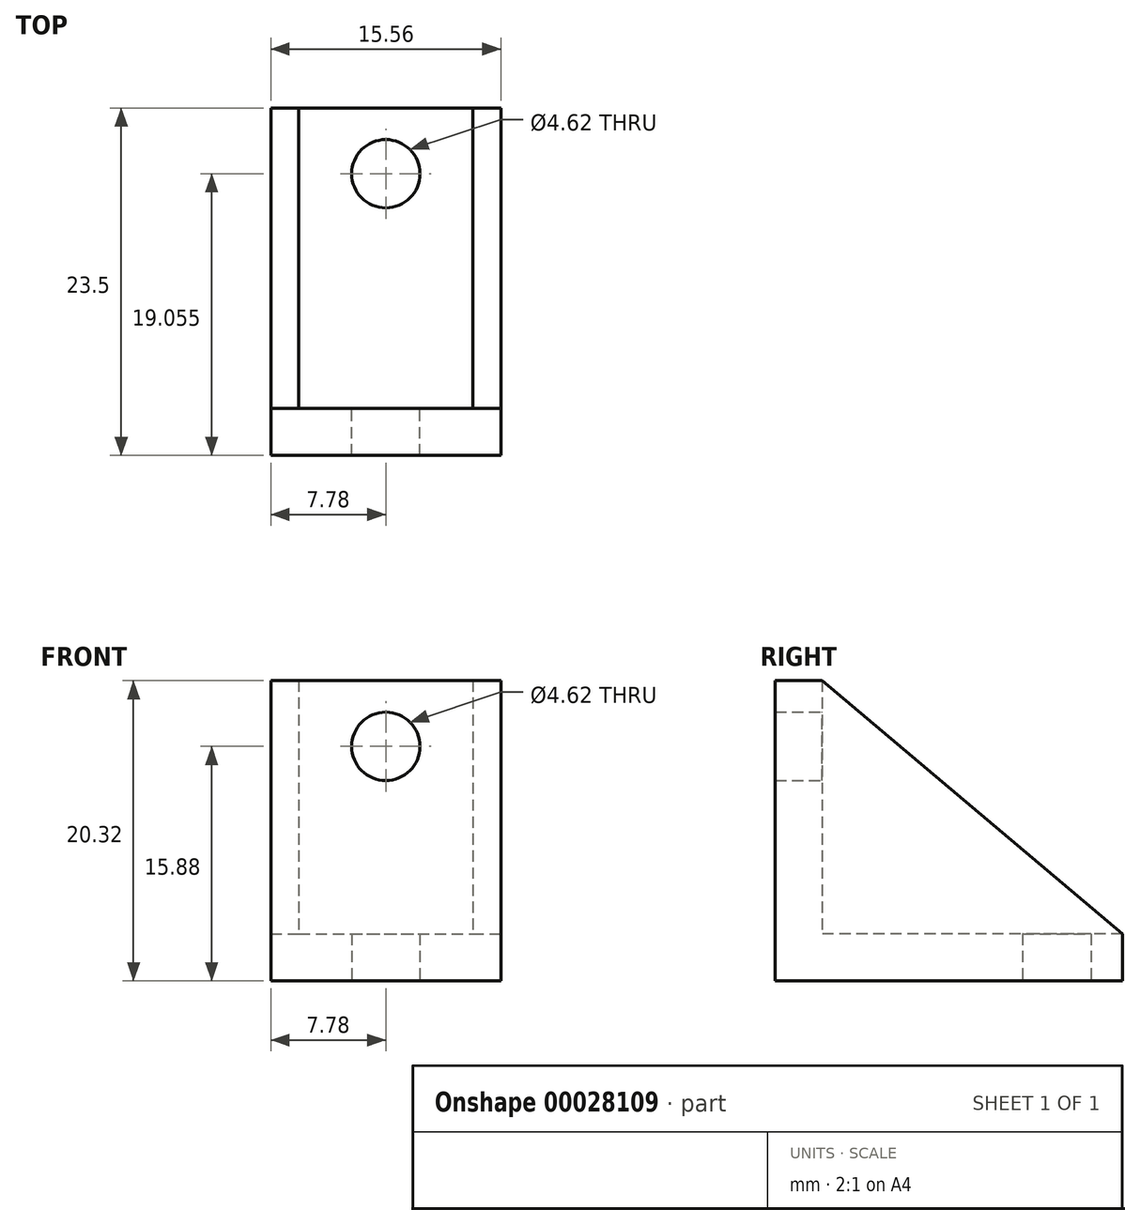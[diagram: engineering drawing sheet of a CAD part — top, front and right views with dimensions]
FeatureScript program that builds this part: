
annotation { "Feature Type Name" : "Feature", "Feature Type Description" : "" }
export const myFeature = defineFeature(function(context is Context, id is Id, definition is map)
    precondition{}
    {
        {
            var Q0;
            Q0=qCreatedBy(makeId("Front.planeOp"),FACE);
            var sketch = newSketch(context, id + "F0", { "sketchPlane" : qUnion([Q0])});
            skLineSegment(sketch, "E0.bottom", {"start": v(-31.66, 5.56) * mm, "end": v(-16.1, 5.56) * mm});
            skLineSegment(sketch, "E0.top", {"start": v(-31.66, -14.76) * mm, "end": v(-16.1, -14.76) * mm});
            skLineSegment(sketch, "E0.left", {"start": v(-31.66, 5.56) * mm, "end": v(-31.66, -14.76) * mm});
            skLineSegment(sketch, "E0.right", {"start": v(-16.1, 5.56) * mm, "end": v(-16.1, -14.76) * mm});
            skLineSegment(sketch, "E1.bottom", {"start": v(-31.66, -14.76) * mm, "end": v(-16.1, -14.76) * mm, "construction": true});
            skLineSegment(sketch, "E1.top", {"start": v(-31.66, -17.93) * mm, "end": v(-16.1, -17.93) * mm, "construction": true});
            skLineSegment(sketch, "E1.left", {"start": v(-31.66, -14.76) * mm, "end": v(-31.66, -17.93) * mm, "construction": true});
            skLineSegment(sketch, "E1.right", {"start": v(-16.1, -14.76) * mm, "end": v(-16.1, -17.93) * mm, "construction": true});
            skLineSegment(sketch, "E2", {"start": v(-23.88, -17.93) * mm, "end": v(-23.88, 1.12) * mm, "construction": true});
            skCircle(sketch, "E3", {"center": v(-23.88, 1.12) * mm, "radius": 2.31 * mm});
            skSolve(sketch);
        }
        {
            var Q0;
            Q0=makeQuery(id+"F0.imprint","IMPRINT",FACE,{"disambiguationData":[TD([[makeQuery(id+"F0.imprint","IMPRINT",EDGE,{"derivedFrom":sQuery(id+"F0.wireOp",EDGE,"E0.bottom")}),-1.0]])]});
            extrude(context, id + "F1", {"entities" : qUnion([Q0]), "depth" : 3.17 * mm});
        }
        {
            var Q0;
            Q0=makeQuery(id+"F1.opExtrude","CAP_FACE",FACE,{"disambiguationData":[OSD([sQuery(id+"F0.wireOp",EDGE,"E0.bottom"),sQuery(id+"F0.wireOp",EDGE,"E0.top"),sQuery(id+"F0.wireOp",EDGE,"E0.left"),sQuery(id+"F0.wireOp",EDGE,"E0.right"),sQuery(id+"F0.wireOp",EDGE,"E3")])],"isStart":true});
            var sketch = newSketch(context, id + "F2", { "sketchPlane" : qUnion([Q0])});
            skLineSegment(sketch, "E4.bottom", {"start": v(31.66, -14.76) * mm, "end": v(16.1, -14.76) * mm});
            skLineSegment(sketch, "E4.top", {"start": v(31.66, -11.58) * mm, "end": v(16.1, -11.58) * mm});
            skLineSegment(sketch, "E4.left", {"start": v(31.66, -14.76) * mm, "end": v(31.66, -11.58) * mm});
            skLineSegment(sketch, "E4.right", {"start": v(16.1, -14.76) * mm, "end": v(16.1, -11.58) * mm});
            skSolve(sketch);
        }
        {
            var Q0;
            Q0=makeQuery(id+"F2.imprint","IMPRINT",FACE,{"disambiguationData":[TD([[makeQuery(id+"F2.imprint","IMPRINT",EDGE,{"derivedFrom":sQuery(id+"F2.wireOp",EDGE,"E4.bottom")}),-1.0]])]});
            extrude(context, id + "F3", {"entities" : qUnion([Q0]), "operationType" : NewBodyOperationType.ADD, "depth" : 20.32 * mm});
        }
        {
            var Q0;
            Q0=makeQuery(id+"F3.boolean.opBoolean","MERGE",FACE,{"derivedFrom":[makeQuery(id+"F1.opExtrude","SWEPT_FACE",FACE,{"disambiguationData":[OSD([sQuery(id+"F0.wireOp",EDGE,"E0.top")])]}),makeQuery(id+"F3.opExtrude","SWEPT_FACE",FACE,{"disambiguationData":[OSD([sQuery(id+"F2.wireOp",EDGE,"E4.bottom")])]})]});
            var sketch = newSketch(context, id + "F4", { "sketchPlane" : qUnion([Q0])});
            skLineSegment(sketch, "E5", {"start": v(-23.88, 3.18) * mm, "end": v(-23.88, -15.88) * mm, "construction": true});
            skPoint(sketch, "E5.endSnap0", {"position": v(-23.88, 3.18) * mm});
            skCircle(sketch, "E6", {"center": v(-23.88, -15.88) * mm, "radius": 2.31 * mm});
            skSolve(sketch);
        }
        {
            var Q0;
            Q0=makeQuery(id+"F4.imprint","IMPRINT",FACE,{"disambiguationData":[TD([[makeQuery(id+"F4.imprint","IMPRINT",EDGE,{"derivedFrom":sQuery(id+"F4.wireOp",EDGE,"E6")}),1.0]])]});
            extrude(context, id + "F5", {"entities" : qUnion([Q0]), "operationType" : NewBodyOperationType.REMOVE, "oppositeDirection" : true, "depth" : 25.4 * mm});
        }
        {
            var Q0;
            Q0=makeQuery(id+"F3.boolean.opBoolean","MERGE",FACE,{"derivedFrom":[makeQuery(id+"F1.opExtrude","SWEPT_FACE",FACE,{"disambiguationData":[OSD([sQuery(id+"F0.wireOp",EDGE,"E0.right")])]}),makeQuery(id+"F3.opExtrude","SWEPT_FACE",FACE,{"disambiguationData":[OSD([sQuery(id+"F2.wireOp",EDGE,"E4.right")])]})]});
            var sketch = newSketch(context, id + "F6", { "sketchPlane" : qUnion([Q0])});
            skLineSegment(sketch, "E7", {"start": v(0, 5.56) * mm, "end": v(20.32, -11.58) * mm});
            skSolve(sketch);
        }
        {
            var Q0;
            Q0=makeQuery(id+"F6.imprint","IMPRINT",FACE,{"disambiguationData":[TD([[makeQuery(id+"F6.imprint","IMPRINT",EDGE,{"derivedFrom":sQuery(id+"F6.wireOp",EDGE,"E7")}),-1.0]])]});
            extrude(context, id + "F7", {"entities" : qUnion([Q0]), "operationType" : NewBodyOperationType.ADD, "oppositeDirection" : true, "depth" : 1.9 * mm});
        }
        {
            var Q0;
            Q0=makeQuery(id+"F3.boolean.opBoolean","MERGE",FACE,{"derivedFrom":[makeQuery(id+"F1.opExtrude","SWEPT_FACE",FACE,{"disambiguationData":[OSD([sQuery(id+"F0.wireOp",EDGE,"E0.left")])]}),makeQuery(id+"F3.opExtrude","SWEPT_FACE",FACE,{"disambiguationData":[OSD([sQuery(id+"F2.wireOp",EDGE,"E4.left")])]})]});
            var sketch = newSketch(context, id + "F8", { "sketchPlane" : qUnion([Q0])});
            skLineSegment(sketch, "E8", {"start": v(-20.32, -11.58) * mm, "end": v(0, 5.56) * mm});
            skSolve(sketch);
        }
        {
            var Q0;
            Q0=makeQuery(id+"F8.imprint","IMPRINT",FACE,{"disambiguationData":[TD([[makeQuery(id+"F8.imprint","IMPRINT",EDGE,{"derivedFrom":sQuery(id+"F8.wireOp",EDGE,"E8")}),-1.0]])]});
            extrude(context, id + "F9", {"entities" : qUnion([Q0]), "operationType" : NewBodyOperationType.ADD, "oppositeDirection" : true, "depth" : 1.9 * mm});
        }
    });
